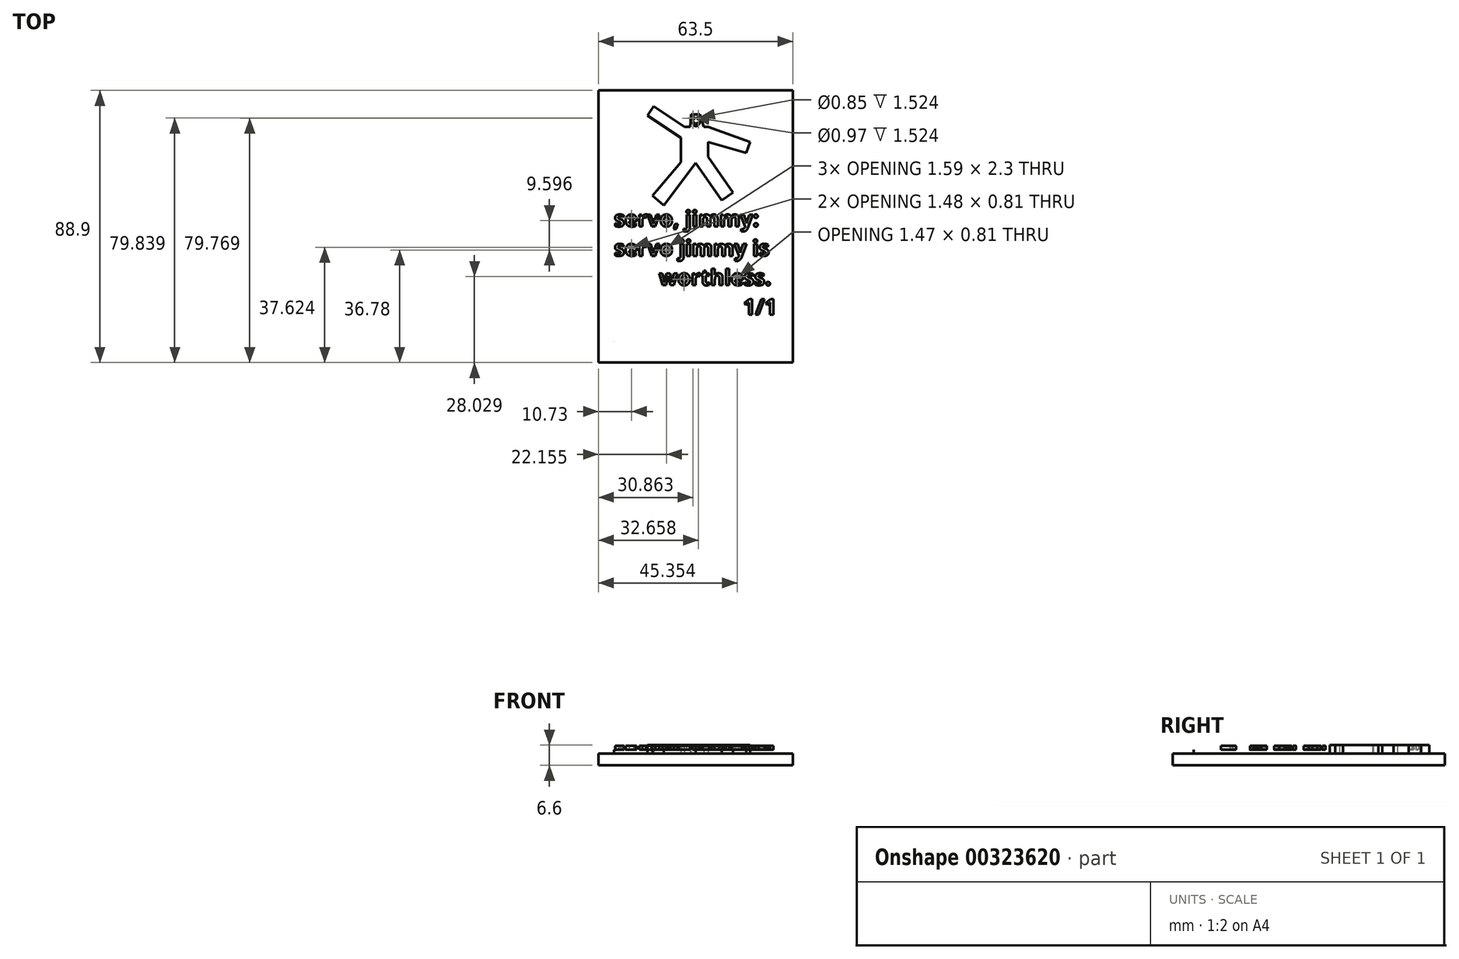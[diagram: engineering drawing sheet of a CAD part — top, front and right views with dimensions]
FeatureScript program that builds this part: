
annotation { "Feature Type Name" : "Feature", "Feature Type Description" : "" }
export const myFeature = defineFeature(function(context is Context, id is Id, definition is map)
    precondition{}
    {
        {
            var Q0;
            Q0=qCreatedBy(makeId("Top.planeOp"),FACE);
            var sketch = newSketch(context, id + "F0", { "sketchPlane" : qUnion([Q0])});
            skLineSegment(sketch, "E0.bottom", {"start": v(31.75, -44.45) * mm, "end": v(-31.75, -44.45) * mm});
            skLineSegment(sketch, "E0.top", {"start": v(31.75, 44.45) * mm, "end": v(-31.75, 44.45) * mm});
            skLineSegment(sketch, "E0.left", {"start": v(31.75, -44.45) * mm, "end": v(31.75, 44.45) * mm});
            skLineSegment(sketch, "E0.right", {"start": v(-31.75, -44.45) * mm, "end": v(-31.75, 44.45) * mm});
            skPoint(sketch, "E0.middle", {"position": v(0, 0) * mm});
            skSolve(sketch);
        }
        {
            var Q0;
            Q0=makeQuery(id+"F0.imprint","IMPRINT",FACE,{"disambiguationData":[TD([[makeQuery(id+"F0.imprint","IMPRINT",EDGE,{"derivedFrom":sQuery(id+"F0.wireOp",EDGE,"E0.bottom")}),-1.0]])]});
            extrude(context, id + "F1", {"entities" : qUnion([Q0]), "depth" : 5.08 * mm});
        }
        {
            var Q0;
            Q0=makeQuery(id+"F1.opExtrude","CAP_FACE",FACE,{"disambiguationData":[OSD([sQuery(id+"F0.wireOp",EDGE,"E0.bottom"),sQuery(id+"F0.wireOp",EDGE,"E0.top"),sQuery(id+"F0.wireOp",EDGE,"E0.left"),sQuery(id+"F0.wireOp",EDGE,"E0.right")])],"isStart":false});
            var sketch = newSketch(context, id + "F2", { "sketchPlane" : qUnion([Q0])});
            skLineSegment(sketch, "E1", {"start": v(0, 20.73) * mm, "end": v(8.52, 8.58) * mm});
            skLineSegment(sketch, "E2", {"start": v(8.52, 8.58) * mm, "end": v(12.15, 11.12) * mm});
            skLineSegment(sketch, "E3", {"start": v(12.15, 11.12) * mm, "end": v(4, 22.73) * mm});
            skLineSegment(sketch, "E4", {"start": v(4, 22.73) * mm, "end": v(4, 32.53) * mm});
            skLineSegment(sketch, "E5", {"start": v(4, 32.53) * mm, "end": v(0, 32.53) * mm});
            skLineSegment(sketch, "E6", {"start": v(0, 32.53) * mm, "end": v(-3.7, 32.53) * mm});
            skLineSegment(sketch, "E7", {"start": v(-3.7, 32.53) * mm, "end": v(-13.72, 39.26) * mm});
            skLineSegment(sketch, "E8", {"start": v(-13.72, 39.26) * mm, "end": v(-15.73, 36.26) * mm});
            skLineSegment(sketch, "E9", {"start": v(-15.73, 36.26) * mm, "end": v(-4.8, 28.92) * mm});
            skLineSegment(sketch, "E10", {"start": v(-4.8, 28.92) * mm, "end": v(-4.8, 21) * mm});
            skLineSegment(sketch, "E11", {"start": v(-4.8, 21) * mm, "end": v(-14.13, 10.02) * mm});
            skLineSegment(sketch, "E12", {"start": v(-14.13, 10.02) * mm, "end": v(-10.37, 6.82) * mm});
            skLineSegment(sketch, "E13", {"start": v(-10.37, 6.82) * mm, "end": v(0, 20.73) * mm});
            skLineSegment(sketch, "E14", {"start": v(4, 32.53) * mm, "end": v(17.8, 27.63) * mm});
            skPoint(sketch, "E14.endSnap0", {"position": v(4, 27.63) * mm});
            skLineSegment(sketch, "E15", {"start": v(17.8, 27.63) * mm, "end": v(16.49, 23.96) * mm});
            skLineSegment(sketch, "E16", {"start": v(16.49, 23.96) * mm, "end": v(4, 27.63) * mm});
            skLineSegment(sketch, "E17", {"start": v(-1.85, 32.53) * mm, "end": v(-1.48, 36.6) * mm});
            skLineSegment(sketch, "E18", {"start": v(-1.48, 36.6) * mm, "end": v(0, 36.6) * mm});
            skLineSegment(sketch, "E19", {"start": v(0, 36.6) * mm, "end": v(1.4, 36.6) * mm});
            skLineSegment(sketch, "E20", {"start": v(1.4, 36.6) * mm, "end": v(2.62, 32.53) * mm});
            skCircle(sketch, "E21", {"center": v(-0.89, 35.32) * mm, "radius": 0.48 * mm});
            skCircle(sketch, "E22", {"center": v(0.9, 35.39) * mm, "radius": 0.42 * mm});
            skFitSpline(sketch, "E23", {"points": [v(-0.85, 34.16) * mm, v(0, 33.57) * mm, v(1.45, 34.3) * mm, v(0.9, 33.2) * mm, v(-0.56, 33.01) * mm, v(-0.85, 34.16) * mm]});
            skSolve(sketch);
        }
        {
            var Q0;
            Q0=makeQuery(id+"F2.imprint","IMPRINT",FACE,{"disambiguationData":[TD([[makeQuery(id+"F2.imprint","IMPRINT",EDGE,{"derivedFrom":sQuery(id+"F2.wireOp",EDGE,"E1")}),1.0]])]});
            var Q1;
            {var subQ0=sQuery(id+"F2.wireOp",EDGE,"E14");Q1=makeQuery(id+"F2.imprint","IMPRINT",FACE,{"disambiguationData":[TD([[makeQuery(id+"F2.imprint","IMPRINT",EDGE,{"derivedFrom":subQ0}),-1.0]])]});}
            var Q2;
            {var subQ0=sQuery(id+"F2.wireOp",EDGE,"E17");Q2=makeQuery(id+"F2.imprint","IMPRINT",FACE,{"disambiguationData":[TD([[makeQuery(id+"F2.imprint","IMPRINT",EDGE,{"derivedFrom":subQ0}),-1.0]])]});}
            extrude(context, id + "F3", {"entities" : qUnion([Q0, Q1, Q2]), "operationType" : NewBodyOperationType.ADD, "depth" : 1.52 * mm});
        }
        {
            var Q0;
            Q0=makeQuery(id+"F2.imprint","IMPRINT",FACE,{"disambiguationData":[TD([[makeQuery(id+"F2.imprint","IMPRINT",EDGE,{"derivedFrom":sQuery(id+"F2.wireOp",EDGE,"E1")}),-1.0]])]});
            var sketch = newSketch(context, id + "F4", { "sketchPlane" : qUnion([Q0])});
            skFitSpline(sketch, "E24", {"points": [v(-26.28, -37.6) * mm, v(-24.66, -36.24) * mm, v(-26, -34.84) * mm, v(-27.95, -36.5) * mm, v(-26.28, -37.6) * mm]});
            skFitSpline(sketch, "E25", {"points": [v(-26.28, -37.6) * mm, v(-24.66, -37.6) * mm, v(-24.66, -38.83) * mm, v(-26.28, -39.8) * mm, v(-27.48, -38.6) * mm, v(-26.28, -37.6) * mm]});
            skLineSegment(sketch, "E26", {"start": v(-26.68, -33.27) * mm, "end": v(-25.12, -41.42) * mm});
            skLineSegment(sketch, "E27", {"start": v(-28.77, -38.13) * mm, "end": v(-22.3, -36.5) * mm});
            skLineSegment(sketch, "E28.bottom", {"start": v(-22.3, -37.31) * mm, "end": v(-30.26, -37.31) * mm});
            skLineSegment(sketch, "E28.top", {"start": v(-22.3, -37.89) * mm, "end": v(-30.26, -37.89) * mm});
            skLineSegment(sketch, "E28.left", {"start": v(-22.3, -37.31) * mm, "end": v(-22.3, -37.89) * mm});
            skLineSegment(sketch, "E28.right", {"start": v(-30.26, -37.31) * mm, "end": v(-30.26, -37.89) * mm});
            skPoint(sketch, "E28.cornerSnap0", {"position": v(-25.53, -37.31) * mm});
            skLineSegment(sketch, "E29.bottom", {"start": v(-25.9, -42.16) * mm, "end": v(-26.65, -42.16) * mm});
            skLineSegment(sketch, "E29.top", {"start": v(-25.9, -33.04) * mm, "end": v(-26.65, -33.04) * mm});
            skLineSegment(sketch, "E29.left", {"start": v(-25.9, -42.16) * mm, "end": v(-25.9, -33.04) * mm});
            skLineSegment(sketch, "E29.right", {"start": v(-26.65, -42.16) * mm, "end": v(-26.65, -33.04) * mm});
            skPoint(sketch, "E29.cornerSnap0", {"position": v(-25.9, -37.34) * mm});
            skSolve(sketch);
        }
        {
            var Q0;
            {var subQ0=sQuery(id+"F4.wireOp",EDGE,"E28.left");Q0=makeQuery(id+"F4.imprint","IMPRINT",FACE,{"disambiguationData":[TD([[makeQuery(id+"F4.imprint","IMPRINT",EDGE,{"derivedFrom":subQ0}),-1.0]])]});}
            var Q1;
            {var subQ0=sQuery(id+"F4.wireOp",EDGE,"E28.right");Q1=makeQuery(id+"F4.imprint","IMPRINT",FACE,{"disambiguationData":[TD([[makeQuery(id+"F4.imprint","IMPRINT",EDGE,{"derivedFrom":subQ0}),1.0]])]});}
            var Q2;
            {var subQ0=sQuery(id+"F4.wireOp",EDGE,"E26");var subQ1=sQuery(id+"F4.wireOp",EDGE,"E24");var subQ2=makeQuery(id+"F4.imprint","INTERSECT",VERTEX,{"disambiguationData":[OD(0.0)],"derivedFrom":[subQ1,subQ0]});Q2=makeQuery(id+"F4.imprint","IMPRINT",FACE,{"disambiguationData":[TD([[makeQuery(id+"F4.imprint","IMPRINT",EDGE,{"disambiguationData":[TD([[subQ2,-1.0]])],"derivedFrom":subQ1}),-1.0]])]});}
            var Q3;
            {var subQ0=sQuery(id+"F4.wireOp",EDGE,"E29.left");var subQ1=sQuery(id+"F4.wireOp",EDGE,"E24");var subQ2=makeQuery(id+"F4.imprint","INTERSECT",VERTEX,{"disambiguationData":[OD(0.0)],"derivedFrom":[subQ1,subQ0]});Q3=makeQuery(id+"F4.imprint","IMPRINT",FACE,{"disambiguationData":[TD([[makeQuery(id+"F4.imprint","IMPRINT",EDGE,{"disambiguationData":[TD([[subQ2,1.0]])],"derivedFrom":subQ1}),-1.0]])]});}
            var Q4;
            {var subQ0=sQuery(id+"F4.wireOp",EDGE,"E29.left");var subQ1=sQuery(id+"F4.wireOp",EDGE,"E24");var subQ2=makeQuery(id+"F4.imprint","INTERSECT",VERTEX,{"disambiguationData":[OD(0.0)],"derivedFrom":[subQ1,subQ0]});Q4=makeQuery(id+"F4.imprint","IMPRINT",FACE,{"disambiguationData":[TD([[makeQuery(id+"F4.imprint","IMPRINT",EDGE,{"disambiguationData":[TD([[subQ2,-1.0]])],"derivedFrom":subQ1}),-1.0]])]});}
            var Q5;
            {var subQ0=sQuery(id+"F4.wireOp",EDGE,"E28.top");var subQ1=sQuery(id+"F4.wireOp",EDGE,"E25");var subQ2=makeQuery(id+"F4.imprint","INTERSECT",VERTEX,{"disambiguationData":[OD(1.0)],"derivedFrom":[subQ1,subQ0]});Q5=makeQuery(id+"F4.imprint","IMPRINT",FACE,{"disambiguationData":[TD([[makeQuery(id+"F4.imprint","IMPRINT",EDGE,{"disambiguationData":[TD([[subQ2,-1.0]])],"derivedFrom":subQ1}),-1.0]])]});}
            var Q6;
            {var subQ0=sQuery(id+"F4.wireOp",EDGE,"E28.top");var subQ1=sQuery(id+"F4.wireOp",EDGE,"E25");var subQ2=makeQuery(id+"F4.imprint","INTERSECT",VERTEX,{"disambiguationData":[OD(1.0)],"derivedFrom":[subQ1,subQ0]});Q6=makeQuery(id+"F4.imprint","IMPRINT",FACE,{"disambiguationData":[TD([[makeQuery(id+"F4.imprint","IMPRINT",EDGE,{"disambiguationData":[TD([[subQ2,-1.0]])],"derivedFrom":subQ1}),1.0]])]});}
            var Q7;
            {var subQ0=sQuery(id+"F4.wireOp",EDGE,"E25");var subQ1=sQuery(id+"F4.wireOp",EDGE,"E24");var subQ2=makeQuery(id+"F4.imprint","INTERSECT",VERTEX,{"disambiguationData":[OD(0.0)],"derivedFrom":[subQ1,subQ0]});Q7=makeQuery(id+"F4.imprint","IMPRINT",FACE,{"disambiguationData":[TD([[makeQuery(id+"F4.imprint","IMPRINT",EDGE,{"disambiguationData":[TD([[subQ2,1.0]])],"derivedFrom":subQ1}),-1.0]])]});}
            var Q8;
            {var subQ0=sQuery(id+"F4.wireOp",EDGE,"E25");var subQ1=sQuery(id+"F4.wireOp",EDGE,"E24");var subQ2=makeQuery(id+"F4.imprint","INTERSECT",VERTEX,{"disambiguationData":[OD(0.0)],"derivedFrom":[subQ1,subQ0]});Q8=makeQuery(id+"F4.imprint","IMPRINT",FACE,{"disambiguationData":[TD([[makeQuery(id+"F4.imprint","IMPRINT",EDGE,{"disambiguationData":[TD([[subQ2,1.0]])],"derivedFrom":subQ1}),1.0]])]});}
            var Q9;
            {var subQ0=sQuery(id+"F4.wireOp",EDGE,"E29.left");var subQ1=sQuery(id+"F4.wireOp",EDGE,"E24");var subQ2=makeQuery(id+"F4.imprint","INTERSECT",VERTEX,{"disambiguationData":[OD(0.0)],"derivedFrom":[subQ1,subQ0]});Q9=makeQuery(id+"F4.imprint","IMPRINT",FACE,{"disambiguationData":[TD([[makeQuery(id+"F4.imprint","IMPRINT",EDGE,{"disambiguationData":[TD([[subQ2,1.0]])],"derivedFrom":subQ1}),1.0]])]});}
            var Q10;
            {var subQ1=sQuery(id+"F4.wireOp",EDGE,"E25");var subQ6=sQuery(id+"F4.wireOp",EDGE,"E24");var subQ9=makeQuery(id+"F4.imprint","INTERSECT",VERTEX,{"disambiguationData":[OD(1.0)],"derivedFrom":[subQ6,subQ1]});Q10=makeQuery(id+"F4.imprint","IMPRINT",FACE,{"disambiguationData":[TD([[makeQuery(id+"F4.imprint","IMPRINT",EDGE,{"disambiguationData":[TD([[subQ9,-1.0]])],"derivedFrom":subQ6}),1.0]])]});}
            var Q11;
            {var subQ0=sQuery(id+"F4.wireOp",EDGE,"E29.left");var subQ1=sQuery(id+"F4.wireOp",EDGE,"E25");var subQ2=makeQuery(id+"F4.imprint","INTERSECT",VERTEX,{"disambiguationData":[OD(0.0)],"derivedFrom":[subQ1,subQ0]});Q11=makeQuery(id+"F4.imprint","IMPRINT",FACE,{"disambiguationData":[TD([[makeQuery(id+"F4.imprint","IMPRINT",EDGE,{"disambiguationData":[TD([[subQ2,-1.0]])],"derivedFrom":subQ1}),1.0]])]});}
            var Q12;
            {var subQ0=sQuery(id+"F4.wireOp",EDGE,"E26");var subQ1=sQuery(id+"F4.wireOp",EDGE,"E24");var subQ2=makeQuery(id+"F4.imprint","INTERSECT",VERTEX,{"disambiguationData":[OD(0.0)],"derivedFrom":[subQ1,subQ0]});Q12=makeQuery(id+"F4.imprint","IMPRINT",FACE,{"disambiguationData":[TD([[makeQuery(id+"F4.imprint","IMPRINT",EDGE,{"disambiguationData":[TD([[subQ2,-1.0]])],"derivedFrom":subQ1}),1.0]])]});}
            var Q13;
            {var subQ0=sQuery(id+"F4.wireOp",EDGE,"E29.left");var subQ1=sQuery(id+"F4.wireOp",EDGE,"E24");var subQ2=makeQuery(id+"F4.imprint","INTERSECT",VERTEX,{"disambiguationData":[OD(0.0)],"derivedFrom":[subQ1,subQ0]});Q13=makeQuery(id+"F4.imprint","IMPRINT",FACE,{"disambiguationData":[TD([[makeQuery(id+"F4.imprint","IMPRINT",EDGE,{"disambiguationData":[TD([[subQ2,-1.0]])],"derivedFrom":subQ1}),1.0]])]});}
            var Q14;
            {var subQ0=sQuery(id+"F4.wireOp",EDGE,"E28.bottom");var subQ1=sQuery(id+"F4.wireOp",EDGE,"E24");var subQ2=makeQuery(id+"F4.imprint","INTERSECT",VERTEX,{"disambiguationData":[OD(1.0)],"derivedFrom":[subQ1,subQ0]});Q14=makeQuery(id+"F4.imprint","IMPRINT",FACE,{"disambiguationData":[TD([[makeQuery(id+"F4.imprint","IMPRINT",EDGE,{"disambiguationData":[TD([[subQ2,-1.0]])],"derivedFrom":subQ1}),1.0]])]});}
            var Q15;
            {var subQ0=sQuery(id+"F4.wireOp",EDGE,"E29.right");var subQ1=sQuery(id+"F4.wireOp",EDGE,"E24");var subQ2=makeQuery(id+"F4.imprint","INTERSECT",VERTEX,{"disambiguationData":[OD(1.0)],"derivedFrom":[subQ1,subQ0]});Q15=makeQuery(id+"F4.imprint","IMPRINT",FACE,{"disambiguationData":[TD([[makeQuery(id+"F4.imprint","IMPRINT",EDGE,{"disambiguationData":[TD([[subQ2,-1.0]])],"derivedFrom":subQ1}),-1.0]])]});}
            var Q16;
            {var subQ0=sQuery(id+"F4.wireOp",EDGE,"E29.left");var subQ1=sQuery(id+"F4.wireOp",EDGE,"E26");var subQ2=makeQuery(id+"F4.imprint","INTERSECT",VERTEX,{"derivedFrom":[subQ1,subQ0]});Q16=makeQuery(id+"F4.imprint","IMPRINT",FACE,{"disambiguationData":[TD([[makeQuery(id+"F4.imprint","IMPRINT",EDGE,{"disambiguationData":[TD([[subQ2,-1.0]])],"derivedFrom":subQ1}),1.0]])]});}
            var Q17;
            {var subQ0=sQuery(id+"F4.wireOp",EDGE,"E29.left");var subQ1=sQuery(id+"F4.wireOp",EDGE,"E26");var subQ2=makeQuery(id+"F4.imprint","INTERSECT",VERTEX,{"derivedFrom":[subQ1,subQ0]});Q17=makeQuery(id+"F4.imprint","IMPRINT",FACE,{"disambiguationData":[TD([[makeQuery(id+"F4.imprint","IMPRINT",EDGE,{"disambiguationData":[TD([[subQ2,-1.0]])],"derivedFrom":subQ1}),-1.0]])]});}
            var Q18;
            {var subQ1=sQuery(id+"F4.wireOp",EDGE,"E24");var subQ5=sQuery(id+"F4.wireOp",EDGE,"E29.right");var subQ6=makeQuery(id+"F4.imprint","INTERSECT",VERTEX,{"disambiguationData":[OD(1.0)],"derivedFrom":[subQ1,subQ5]});Q18=makeQuery(id+"F4.imprint","IMPRINT",FACE,{"disambiguationData":[TD([[makeQuery(id+"F4.imprint","IMPRINT",EDGE,{"disambiguationData":[TD([[subQ6,-1.0]])],"derivedFrom":subQ1}),1.0]])]});}
            var Q19;
            {var subQ0=sQuery(id+"F4.wireOp",EDGE,"E28.bottom");var subQ1=sQuery(id+"F4.wireOp",EDGE,"E26");var subQ2=makeQuery(id+"F4.imprint","INTERSECT",VERTEX,{"derivedFrom":[subQ1,subQ0]});Q19=makeQuery(id+"F4.imprint","IMPRINT",FACE,{"disambiguationData":[TD([[makeQuery(id+"F4.imprint","IMPRINT",EDGE,{"disambiguationData":[TD([[subQ2,-1.0]])],"derivedFrom":subQ1}),1.0]])]});}
            var Q20;
            {var subQ0=sQuery(id+"F4.wireOp",EDGE,"E29.top");Q20=makeQuery(id+"F4.imprint","IMPRINT",FACE,{"disambiguationData":[TD([[makeQuery(id+"F4.imprint","IMPRINT",EDGE,{"derivedFrom":subQ0}),1.0]])]});}
            var Q21;
            {var subQ0=sQuery(id+"F4.wireOp",EDGE,"E26");var subQ1=sQuery(id+"F4.wireOp",EDGE,"E24");var subQ2=makeQuery(id+"F4.imprint","INTERSECT",VERTEX,{"disambiguationData":[OD(1.0)],"derivedFrom":[subQ1,subQ0]});Q21=makeQuery(id+"F4.imprint","IMPRINT",FACE,{"disambiguationData":[TD([[makeQuery(id+"F4.imprint","IMPRINT",EDGE,{"disambiguationData":[TD([[subQ2,-1.0]])],"derivedFrom":subQ1}),-1.0]])]});}
            var Q22;
            {var subQ0=sQuery(id+"F4.wireOp",EDGE,"E29.left");var subQ1=sQuery(id+"F4.wireOp",EDGE,"E24");var subQ2=makeQuery(id+"F4.imprint","INTERSECT",VERTEX,{"disambiguationData":[OD(1.0)],"derivedFrom":[subQ1,subQ0]});Q22=makeQuery(id+"F4.imprint","IMPRINT",FACE,{"disambiguationData":[TD([[makeQuery(id+"F4.imprint","IMPRINT",EDGE,{"disambiguationData":[TD([[subQ2,-1.0]])],"derivedFrom":subQ1}),1.0]])]});}
            var Q23;
            {var subQ0=sQuery(id+"F4.wireOp",EDGE,"E26");var subQ1=sQuery(id+"F4.wireOp",EDGE,"E24");var subQ2=makeQuery(id+"F4.imprint","INTERSECT",VERTEX,{"disambiguationData":[OD(1.0)],"derivedFrom":[subQ1,subQ0]});Q23=makeQuery(id+"F4.imprint","IMPRINT",FACE,{"disambiguationData":[TD([[makeQuery(id+"F4.imprint","IMPRINT",EDGE,{"disambiguationData":[TD([[subQ2,-1.0]])],"derivedFrom":subQ1}),1.0]])]});}
            var Q24;
            {var subQ0=sQuery(id+"F4.wireOp",EDGE,"E29.left");var subQ1=sQuery(id+"F4.wireOp",EDGE,"E25");var subQ2=makeQuery(id+"F4.imprint","INTERSECT",VERTEX,{"disambiguationData":[OD(1.0)],"derivedFrom":[subQ1,subQ0]});Q24=makeQuery(id+"F4.imprint","IMPRINT",FACE,{"disambiguationData":[TD([[makeQuery(id+"F4.imprint","IMPRINT",EDGE,{"disambiguationData":[TD([[subQ2,-1.0]])],"derivedFrom":subQ1}),-1.0]])]});}
            var Q25;
            {var subQ5=sQuery(id+"F4.wireOp",EDGE,"E29.bottom");Q25=makeQuery(id+"F4.imprint","IMPRINT",FACE,{"disambiguationData":[TD([[makeQuery(id+"F4.imprint","IMPRINT",EDGE,{"derivedFrom":subQ5}),-1.0]])]});}
            var Q26;
            {var subQ0=sQuery(id+"F4.wireOp",EDGE,"E29.right");var subQ1=sQuery(id+"F4.wireOp",EDGE,"E25");var subQ2=makeQuery(id+"F4.imprint","INTERSECT",VERTEX,{"disambiguationData":[OD(0.0)],"derivedFrom":[subQ1,subQ0]});Q26=makeQuery(id+"F4.imprint","IMPRINT",FACE,{"disambiguationData":[TD([[makeQuery(id+"F4.imprint","IMPRINT",EDGE,{"disambiguationData":[TD([[subQ2,-1.0]])],"derivedFrom":subQ1}),-1.0]])]});}
            var Q27;
            {var subQ0=sQuery(id+"F4.wireOp",EDGE,"E26");var subQ1=sQuery(id+"F4.wireOp",EDGE,"E25");var subQ2=makeQuery(id+"F4.imprint","INTERSECT",VERTEX,{"disambiguationData":[OD(0.0)],"derivedFrom":[subQ1,subQ0]});Q27=makeQuery(id+"F4.imprint","IMPRINT",FACE,{"disambiguationData":[TD([[makeQuery(id+"F4.imprint","IMPRINT",EDGE,{"disambiguationData":[TD([[subQ2,-1.0]])],"derivedFrom":subQ1}),-1.0]])]});}
            var Q28;
            {var subQ0=sQuery(id+"F4.wireOp",EDGE,"E26");var subQ1=sQuery(id+"F4.wireOp",EDGE,"E25");var subQ2=makeQuery(id+"F4.imprint","INTERSECT",VERTEX,{"disambiguationData":[OD(0.0)],"derivedFrom":[subQ1,subQ0]});Q28=makeQuery(id+"F4.imprint","IMPRINT",FACE,{"disambiguationData":[TD([[makeQuery(id+"F4.imprint","IMPRINT",EDGE,{"disambiguationData":[TD([[subQ2,1.0]])],"derivedFrom":subQ1}),-1.0]])]});}
            var Q29;
            {var subQ0=sQuery(id+"F4.wireOp",EDGE,"E29.right");var subQ1=sQuery(id+"F4.wireOp",EDGE,"E24");var subQ2=makeQuery(id+"F4.imprint","INTERSECT",VERTEX,{"disambiguationData":[OD(0.0)],"derivedFrom":[subQ1,subQ0]});Q29=makeQuery(id+"F4.imprint","IMPRINT",FACE,{"disambiguationData":[TD([[makeQuery(id+"F4.imprint","IMPRINT",EDGE,{"disambiguationData":[TD([[subQ2,-1.0]])],"derivedFrom":subQ1}),1.0]])]});}
            var Q30;
            {var subQ0=sQuery(id+"F4.wireOp",EDGE,"E27");var subQ1=sQuery(id+"F4.wireOp",EDGE,"E24");var subQ2=makeQuery(id+"F4.imprint","INTERSECT",VERTEX,{"disambiguationData":[OD(0.0)],"derivedFrom":[subQ1,subQ0]});Q30=makeQuery(id+"F4.imprint","IMPRINT",FACE,{"disambiguationData":[TD([[makeQuery(id+"F4.imprint","IMPRINT",EDGE,{"disambiguationData":[TD([[subQ2,-1.0]])],"derivedFrom":subQ1}),1.0]])]});}
            var Q31;
            {var subQ0=sQuery(id+"F4.wireOp",EDGE,"E27");var subQ1=sQuery(id+"F4.wireOp",EDGE,"E24");var subQ2=makeQuery(id+"F4.imprint","INTERSECT",VERTEX,{"disambiguationData":[OD(0.0)],"derivedFrom":[subQ1,subQ0]});Q31=makeQuery(id+"F4.imprint","IMPRINT",FACE,{"disambiguationData":[TD([[makeQuery(id+"F4.imprint","IMPRINT",EDGE,{"disambiguationData":[TD([[subQ2,1.0]])],"derivedFrom":subQ1}),1.0]])]});}
            extrude(context, id + "F5", {"entities" : qUnion([Q0, Q1, Q2, Q3, Q4, Q5, Q6, Q7, Q8, Q9, Q10, Q11, Q12, Q13, Q14, Q15, Q16, Q17, Q18, Q19, Q20, Q21, Q22, Q23, Q24, Q25, Q26, Q27, Q28, Q29, Q30, Q31]), "operationType" : NewBodyOperationType.REMOVE, "oppositeDirection" : true, "depth" : 1.27 * mm});
        }
        {
            var Q0;
            Q0=makeQuery(id+"F2.imprint","IMPRINT",FACE,{"disambiguationData":[TD([[makeQuery(id+"F2.imprint","IMPRINT",EDGE,{"derivedFrom":sQuery(id+"F2.wireOp",EDGE,"E1")}),-1.0]])]});
            var sketch = newSketch(context, id + "F6", { "sketchPlane" : qUnion([Q0])});
            skText(sketch, "E30", { "text": "servo, jimmy:\nservo jimmy is\n        worthless.    \n                       1/1", "fontName": "OpenSans-Bold.ttf"});
            const initialGuessF6  = {"E30": [-0.02667, 0, 1, 0, 0.00508]};
            skSetInitialGuess(sketch, initialGuessF6);
            skSolve(sketch);
        }
        {
            var Q0;
            Q0 = qSketchRegion(id + "F6", true);
            extrude(context, id + "F7", {"entities" : qUnion([Q0]), "operationType" : NewBodyOperationType.ADD, "depth" : 1.27 * mm});
        }
    });
